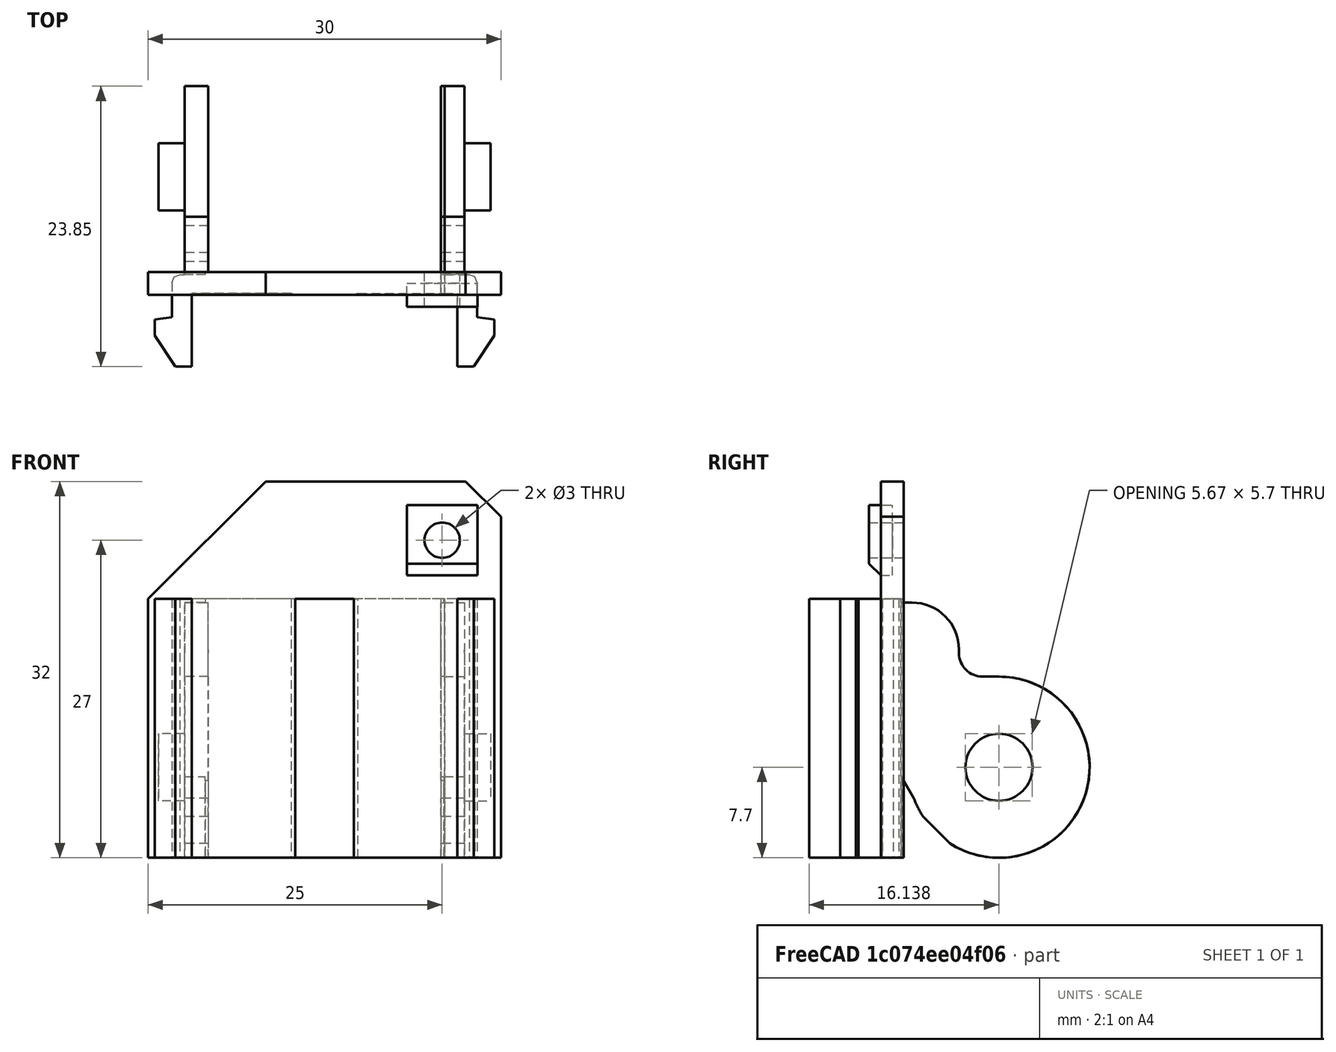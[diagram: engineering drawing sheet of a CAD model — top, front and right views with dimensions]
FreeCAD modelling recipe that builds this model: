
FCSTD DOCUMENT  (FreeCAD 0.18R14555 (Git shallow))
Label: extruder-dragchain-bottom
License: All rights reserved
LicenseURL: http://en.wikipedia.org/wiki/All_rights_reserved
objects: Part::Chamfer×3, Part::Feature×2, Part::Box×2, Part::Cylinder×2, Part::Cut×2
note: 11 computed .brp shape members not serialized (recipe doc carries the construction recipe); baked Part::Feature solids carry a one-line shape summary decoded from their .brp

FEATURE [Part::Feature] Fusion010001001  label="Fusion012"
  Placement = pos=(-11.9,17.05,-10.3) rot=(0,0,1;0rad)
  shape: bbox 28.86 x 23.85 x 22 mm, 120 faces, 4 solids (baked)
FEATURE [Part::Box] Box  label="Cube"
  AttacherType = Attacher::AttachEngine3D
  Height = 32
  Length = 30
  Placement = pos=(-15,0,-22) rot=(0,0,1;0rad)
  Width = 1.95
FEATURE [Part::Cylinder] Cylinder001
  Angle = 360
  AttacherType = Attacher::AttachEngine3D
  Height = 2
  Placement = pos=(10,-1.1e-15,5) rot=(-1,0,0;1.5708rad)
  Radius = 1.5
FEATURE [Part::Feature] Fusion010001001001  label="Fusion013"
  Placement = pos=(-11.9,17.05,-10.3) rot=(0,0,1;0rad)
  shape: bbox 28.86 x 23.85 x 22 mm, 120 faces, 4 solids (baked)
FEATURE [Part::Chamfer] Chamfer
  Base = -> Box
  Edges = 1 edges r=10: [Edge2]
FEATURE [Part::Chamfer] Chamfer001
  Base = -> Chamfer
  Edges = 1 edges r=3: [Edge15]
FEATURE [Part::Cut] Cut
  Base = -> Chamfer001
  Tool = -> Cylinder001
FEATURE [Part::Box] Box001  label="Cube001"
  AttacherType = Attacher::AttachEngine3D
  Height = 6
  Length = 6
  Placement = pos=(7,-1,2) rot=(0,0,1;0rad)
  Width = 2
FEATURE [Part::Cylinder] Cylinder
  Angle = 360
  AttacherType = Attacher::AttachEngine3D
  Height = 10
  Placement = pos=(10,-1,5) rot=(-1,0,0;1.5708rad)
  Radius = 1.5
FEATURE [Part::Chamfer] Chamfer002
  Base = -> Box001
  Edges = 1 edges r=1: [Edge9]
FEATURE [Part::Cut] Cut001
  Base = -> Chamfer002
  Tool = -> Cylinder
